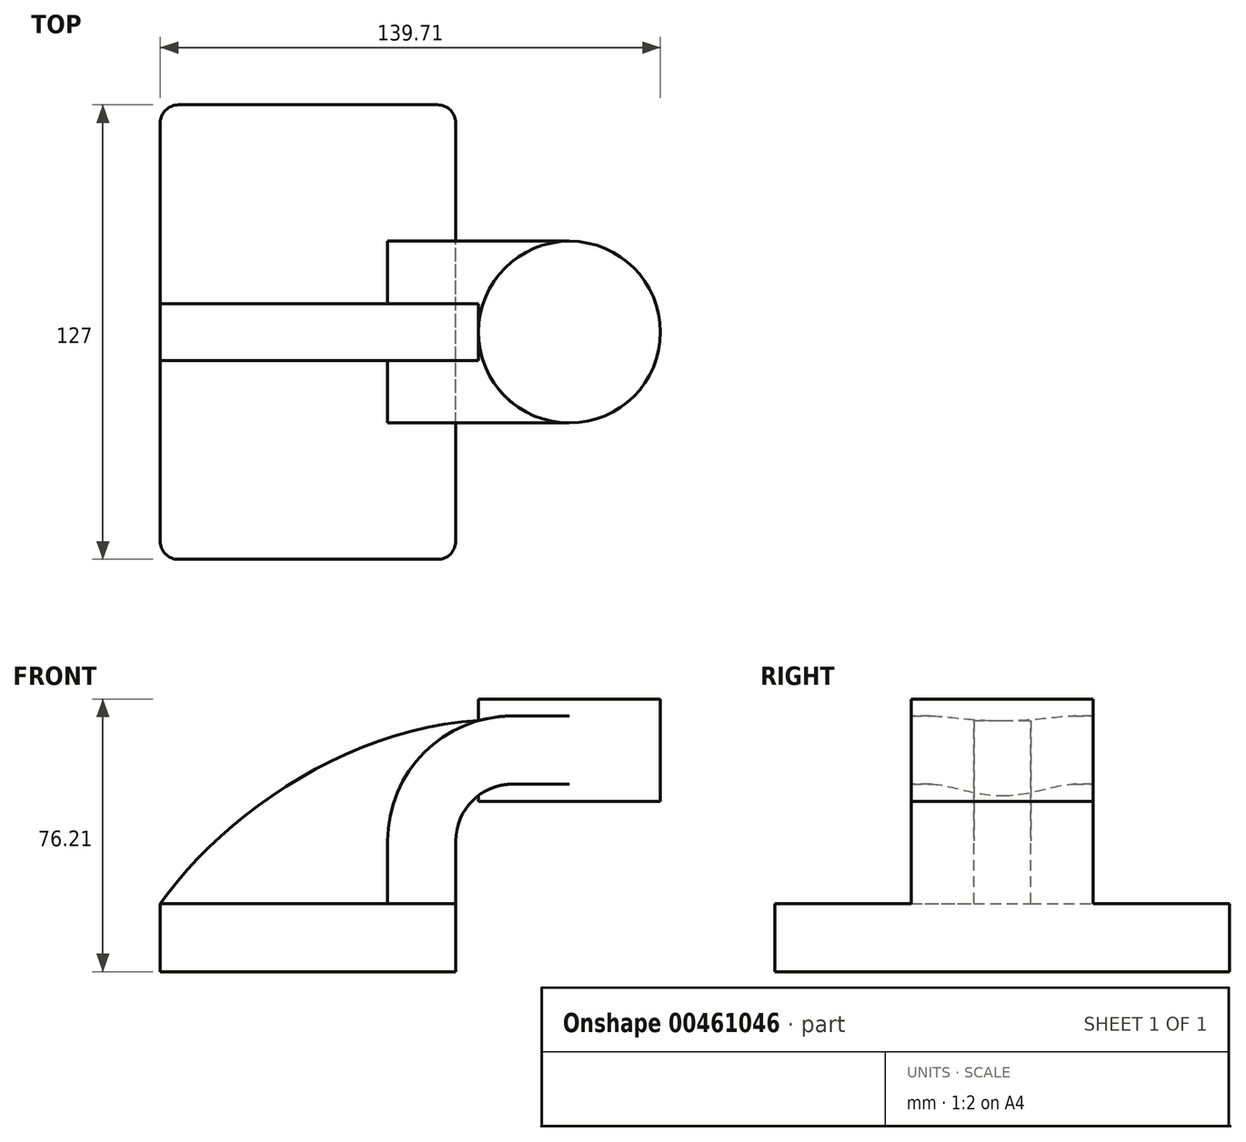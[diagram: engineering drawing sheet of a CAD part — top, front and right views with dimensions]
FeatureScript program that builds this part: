
annotation { "Feature Type Name" : "Feature", "Feature Type Description" : "" }
export const myFeature = defineFeature(function(context is Context, id is Id, definition is map)
    precondition{}
    {
        {
            var Q0;
            Q0=qCreatedBy(makeId("Front.planeOp"),FACE);
            var sketch = newSketch(context, id + "F0", { "sketchPlane" : qUnion([Q0])});
            skLineSegment(sketch, "E0.bottom", {"start": v(41.28, -9.52) * mm, "end": v(-41.28, -9.53) * mm});
            skLineSegment(sketch, "E0.top", {"start": v(41.28, 9.53) * mm, "end": v(-41.28, 9.53) * mm});
            skLineSegment(sketch, "E0.left", {"start": v(41.28, -9.52) * mm, "end": v(41.28, 9.53) * mm});
            skLineSegment(sketch, "E0.right", {"start": v(-41.28, -9.53) * mm, "end": v(-41.28, 9.53) * mm});
            skPoint(sketch, "E0.middle", {"position": v(0, 0) * mm});
            skLineSegment(sketch, "E1.bottom", {"start": v(98.43, 38.1) * mm, "end": v(47.63, 38.1) * mm});
            skLineSegment(sketch, "E1.top", {"start": v(98.43, 66.68) * mm, "end": v(47.63, 66.68) * mm});
            skLineSegment(sketch, "E1.left", {"start": v(98.43, 38.1) * mm, "end": v(98.43, 66.68) * mm});
            skLineSegment(sketch, "E1.right", {"start": v(47.63, 38.1) * mm, "end": v(47.63, 66.68) * mm});
            skPoint(sketch, "E1.middle", {"position": v(73.03, 52.39) * mm});
            skLineSegment(sketch, "E2", {"start": v(41.28, 9.53) * mm, "end": v(41.28, 27) * mm});
            skArc(sketch, "E3", {"start": v(41.27, 27) * mm, "mid": v(45.92, 38.23) * mm, "end": v(57.15, 42.88) * mm});
            skLineSegment(sketch, "E4", {"start": v(57.15, 42.88) * mm, "end": v(73.03, 42.88) * mm});
            skLineSegment(sketch, "E5.0", {"start": v(57.15, 61.93) * mm, "end": v(73.03, 61.93) * mm});
            skArc(sketch, "E5.1", {"start": v(22.23, 27) * mm, "mid": v(32.45, 51.7) * mm, "end": v(57.15, 61.93) * mm});
            skLineSegment(sketch, "E5.2", {"start": v(22.22, 9.53) * mm, "end": v(22.22, 27) * mm});
            skLineSegment(sketch, "E6", {"start": v(73.03, 38.1) * mm, "end": v(73.03, 66.68) * mm});
            skFitSpline(sketch, "E7", {"points": [v(-41.28, 9.52) * mm, v(47.63, 60.6) * mm], "startDerivative": vector(51.7, 72.99) * mm, "endDerivative": vector(110.07, 5.74) * mm});
            skSolve(sketch);
        }
        {
            var Q0;
            Q0=makeQuery(id+"F0.imprint","IMPRINT",FACE,{"disambiguationData":[TD([[makeQuery(id+"F0.imprint","IMPRINT",EDGE,{"derivedFrom":sQuery(id+"F0.wireOp",EDGE,"E0.bottom")}),-1.0]])]});
            extrude(context, id + "F1", {"entities" : qUnion([Q0]), "endBound" : BoundingType.SYMMETRIC, "depth" : 127 * mm});
        }
        {
            var Q0;
            {var subQ1=sQuery(id+"F0.wireOp",EDGE,"E4");Q0=makeQuery(id+"F0.imprint","IMPRINT",FACE,{"disambiguationData":[TD([[makeQuery(id+"F0.imprint","IMPRINT",EDGE,{"derivedFrom":subQ1}),1.0]])]});}
            var Q1;
            {var subQ1=sQuery(id+"F0.wireOp",EDGE,"E2");Q1=makeQuery(id+"F0.imprint","IMPRINT",FACE,{"disambiguationData":[TD([[makeQuery(id+"F0.imprint","IMPRINT",EDGE,{"derivedFrom":subQ1}),1.0]])]});}
            extrude(context, id + "F2", {"entities" : qUnion([Q0, Q1]), "operationType" : NewBodyOperationType.ADD, "endBound" : BoundingType.SYMMETRIC, "depth" : 50.8 * mm, "hasSecondDirection" : true, "secondDirectionOppositeDirection" : true, "secondDirectionDepth" : 50.8 * mm});
        }
        {
            var Q0;
            {var subQ2=sQuery(id+"F0.wireOp",EDGE,"E5.2");Q0=makeQuery(id+"F0.imprint","IMPRINT",FACE,{"disambiguationData":[TD([[makeQuery(id+"F0.imprint","IMPRINT",EDGE,{"derivedFrom":subQ2}),1.0]])]});}
            extrude(context, id + "F3", {"entities" : qUnion([Q0]), "operationType" : NewBodyOperationType.ADD, "endBound" : BoundingType.SYMMETRIC, "depth" : 15.88 * mm});
        }
        {
            var Q0;
            {var subQ4=sQuery(id+"F0.wireOp",EDGE,"E1.left");Q0=makeQuery(id+"F0.imprint","IMPRINT",FACE,{"disambiguationData":[TD([[makeQuery(id+"F0.imprint","IMPRINT",EDGE,{"derivedFrom":subQ4}),1.0]])]});}
            var Q1;
            Q1=sQuery(id+"F0.wireOp",EDGE,"E6");
            revolve(context, id + "F4", {"operationType" : NewBodyOperationType.ADD, "entities" : qUnion([Q0]), "axis" : qUnion([Q1]), "revolveType" : RevolveType.FULL});
        }
        {
            var Q0;
            Q0=makeQuery(id+"F1.opExtrude","CAP_EDGE",EDGE,{"disambiguationData":[OSD([sQuery(id+"F0.wireOp",EDGE,"E0.right")])],"isStart":false});
            var Q1;
            Q1=makeQuery(id+"F1.opExtrude","CAP_EDGE",EDGE,{"disambiguationData":[OSD([sQuery(id+"F0.wireOp",EDGE,"E0.right")])],"isStart":true});
            var Q2;
            Q2=makeQuery(id+"F1.opExtrude","CAP_EDGE",EDGE,{"disambiguationData":[OSD([sQuery(id+"F0.wireOp",EDGE,"E0.left")])],"isStart":true});
            var Q3;
            Q3=makeQuery(id+"F1.opExtrude","CAP_EDGE",EDGE,{"disambiguationData":[OSD([sQuery(id+"F0.wireOp",EDGE,"E0.left")])],"isStart":false});
            fillet(context, id + "F5", {"entities" : qUnion([Q0, Q1, Q2, Q3]), "radius" : 5.08 * mm, "tangentPropagation" : true, "allowEdgeOverflow" : false});
        }
    });
